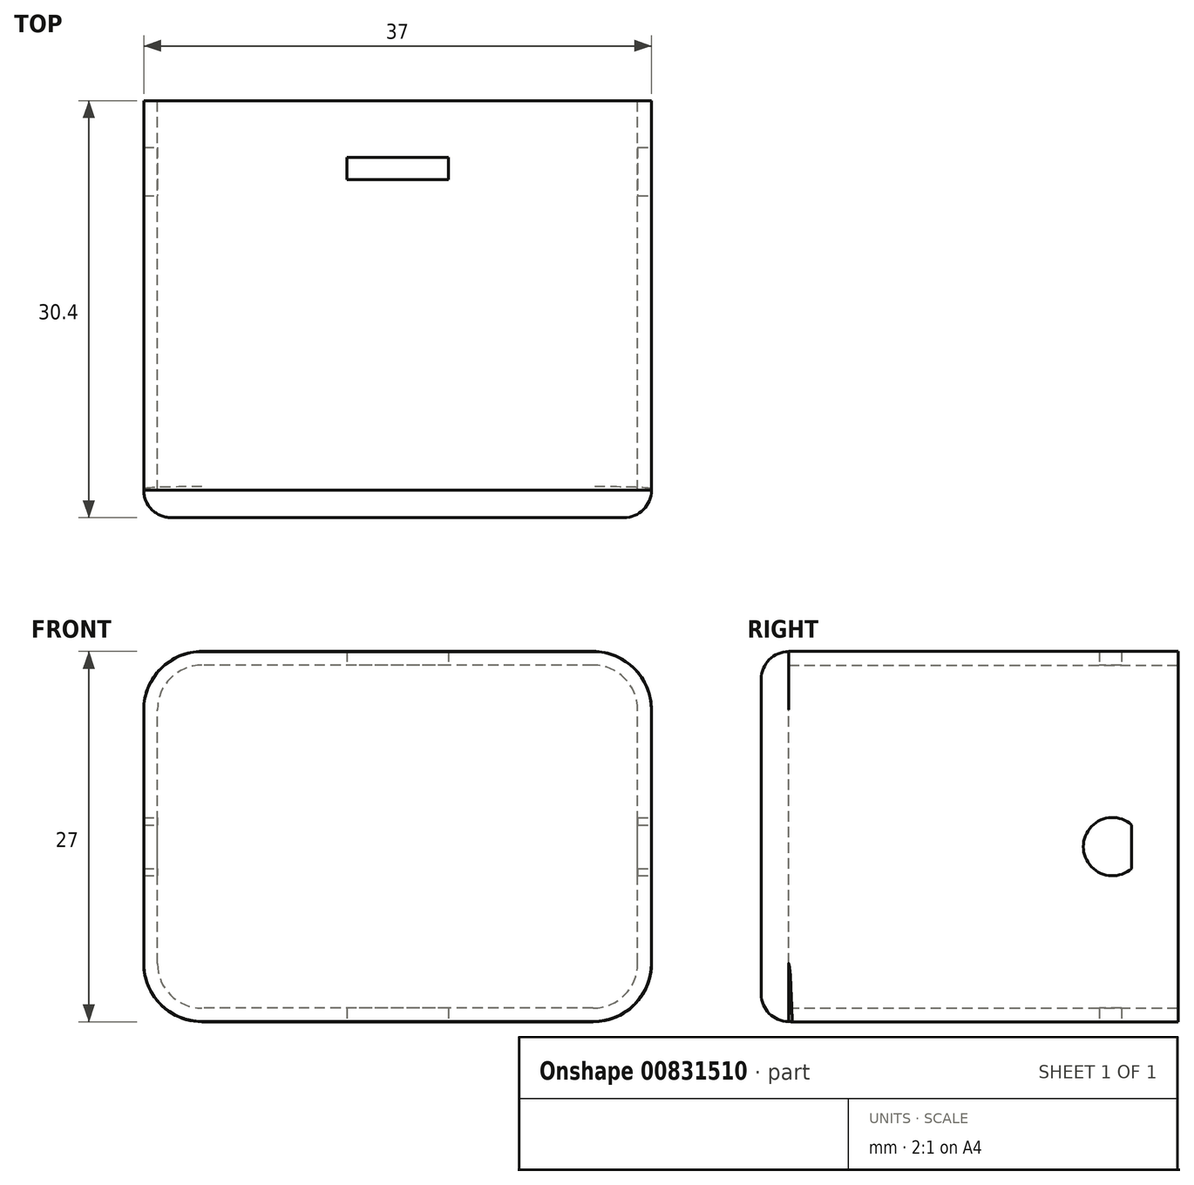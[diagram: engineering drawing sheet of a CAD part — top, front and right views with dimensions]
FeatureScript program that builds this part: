
annotation { "Feature Type Name" : "Feature", "Feature Type Description" : "" }
export const myFeature = defineFeature(function(context is Context, id is Id, definition is map)
    precondition{}
    {
        {
            var Q0;
            Q0=qCreatedBy(makeId("Front.planeOp"),FACE);
            var sketch = newSketch(context, id + "F0", { "sketchPlane" : qUnion([Q0])});
            skLineSegment(sketch, "E0.bottom", {"start": v(14.25, -12.5) * mm, "end": v(-14.25, -12.5) * mm});
            skLineSegment(sketch, "E0.top", {"start": v(14.25, 12.5) * mm, "end": v(-14.25, 12.5) * mm});
            skLineSegment(sketch, "E0.left", {"start": v(17.5, -9.25) * mm, "end": v(17.5, 9.25) * mm});
            skLineSegment(sketch, "E0.right", {"start": v(-17.5, -9.25) * mm, "end": v(-17.5, 9.25) * mm});
            skPoint(sketch, "E0.middle", {"position": v(0, 0) * mm});
            skPoint(sketch, "E1.visualSharp", {"position": v(-17.5, 12.5) * mm});
            skArc(sketch, "E1.filletArc", {"start": v(-14.25, 12.5) * mm, "mid": v(-16.55, 11.55) * mm, "end": v(-17.5, 9.25) * mm});
            skPoint(sketch, "E2.visualSharp", {"position": v(-17.5, -12.5) * mm});
            skArc(sketch, "E2.filletArc", {"start": v(-17.5, -9.25) * mm, "mid": v(-16.55, -11.55) * mm, "end": v(-14.25, -12.5) * mm});
            skPoint(sketch, "E3.visualSharp", {"position": v(17.5, -12.5) * mm});
            skArc(sketch, "E3.filletArc", {"start": v(14.25, -12.5) * mm, "mid": v(16.55, -11.55) * mm, "end": v(17.5, -9.25) * mm});
            skPoint(sketch, "E4.visualSharp", {"position": v(17.5, 12.5) * mm});
            skArc(sketch, "E4.filletArc", {"start": v(17.5, 9.25) * mm, "mid": v(16.55, 11.55) * mm, "end": v(14.25, 12.5) * mm});
            skLineSegment(sketch, "E5.0", {"start": v(14.25, -13.5) * mm, "end": v(-14.25, -13.5) * mm});
            skArc(sketch, "E5.1", {"start": v(-18.5, -9.25) * mm, "mid": v(-17.26, -12.26) * mm, "end": v(-14.25, -13.5) * mm});
            skArc(sketch, "E5.2", {"start": v(14.25, -13.5) * mm, "mid": v(17.26, -12.26) * mm, "end": v(18.5, -9.25) * mm});
            skLineSegment(sketch, "E5.3", {"start": v(-18.5, -9.25) * mm, "end": v(-18.5, 9.25) * mm});
            skLineSegment(sketch, "E5.4", {"start": v(18.5, -9.25) * mm, "end": v(18.5, 9.25) * mm});
            skArc(sketch, "E5.5", {"start": v(18.5, 9.25) * mm, "mid": v(17.26, 12.26) * mm, "end": v(14.25, 13.5) * mm});
            skLineSegment(sketch, "E5.6", {"start": v(14.25, 13.5) * mm, "end": v(-14.25, 13.5) * mm});
            skArc(sketch, "E5.7", {"start": v(-14.25, 13.5) * mm, "mid": v(-17.26, 12.26) * mm, "end": v(-18.5, 9.25) * mm});
            skSolve(sketch);
        }
        {
            var Q0;
            Q0 = qSketchRegion(id + "F0", true);
            extrude(context, id + "F1", {"entities" : qUnion([Q0]), "depth" : 25 * mm, "offsetDistance" : 25 * mm});
        }
        {
            var Q0;
            Q0=makeQuery(id+"F1.opExtrude","SWEPT_FACE",FACE,{"disambiguationData":[OSD([sQuery(id+"F0.wireOp",EDGE,"E5.0")])]});
            var sketch = newSketch(context, id + "F2", { "sketchPlane" : qUnion([Q0])});
            skLineSegment(sketch, "E6.bottom", {"start": v(3.7, 0.74) * mm, "end": v(-3.7, 0.74) * mm});
            skLineSegment(sketch, "E6.top", {"start": v(3.7, 2.34) * mm, "end": v(-3.7, 2.34) * mm});
            skLineSegment(sketch, "E6.left", {"start": v(3.7, 0.74) * mm, "end": v(3.7, 2.34) * mm});
            skLineSegment(sketch, "E6.right", {"start": v(-3.7, 0.74) * mm, "end": v(-3.7, 2.34) * mm});
            skPoint(sketch, "E6.middle", {"position": v(0, 1.54) * mm});
            skSolve(sketch);
        }
        {
            var Q0;
            Q0=makeQuery(id+"F2.imprint","IMPRINT",FACE,{"disambiguationData":[TD([[makeQuery(id+"F2.imprint","IMPRINT",EDGE,{"derivedFrom":sQuery(id+"F2.wireOp",EDGE,"E6.bottom")}),-1.0]])]});
            extrude(context, id + "F3", {"entities" : qUnion([Q0]), "operationType" : NewBodyOperationType.REMOVE, "endBound" : BoundingType.THROUGH_ALL, "oppositeDirection" : true, "depth" : 25 * mm, "offsetDistance" : 25 * mm});
        }
        {
            var Q0;
            Q0=qCreatedBy(makeId("Front.planeOp"),FACE);
            cPlane(context, id + "F4", {"entities" : qUnion([Q0]), "cplaneType" : CPlaneType.OFFSET, "offset" : 25 * mm, "width" : 150 * mm, "height" : 150 * mm});
        }
        {
            var Q0;
            Q0=qCreatedBy(id+"F4.planeOp",FACE);
            var sketch = newSketch(context, id + "F5", { "sketchPlane" : qUnion([Q0])});
            skLineSegment(sketch, "E7.bottom", {"start": v(14.25, -13.48) * mm, "end": v(-14.25, -13.48) * mm});
            skLineSegment(sketch, "E7.top", {"start": v(14.25, 13.48) * mm, "end": v(-14.25, 13.48) * mm});
            skLineSegment(sketch, "E7.left", {"start": v(18.5, -9.23) * mm, "end": v(18.5, 9.23) * mm});
            skLineSegment(sketch, "E7.right", {"start": v(-18.5, -9.23) * mm, "end": v(-18.5, 9.23) * mm});
            skPoint(sketch, "E7.middle", {"position": v(0, 0) * mm});
            skPoint(sketch, "E8.visualSharp", {"position": v(-18.5, 13.48) * mm});
            skArc(sketch, "E8.filletArc", {"start": v(-14.25, 13.48) * mm, "mid": v(-17.26, 12.24) * mm, "end": v(-18.5, 9.23) * mm});
            skPoint(sketch, "E9.visualSharp", {"position": v(18.5, 13.48) * mm});
            skArc(sketch, "E9.filletArc", {"start": v(18.5, 9.23) * mm, "mid": v(17.26, 12.24) * mm, "end": v(14.25, 13.48) * mm});
            skPoint(sketch, "E10.visualSharp", {"position": v(18.5, -13.48) * mm});
            skArc(sketch, "E10.filletArc", {"start": v(14.25, -13.48) * mm, "mid": v(17.26, -12.24) * mm, "end": v(18.5, -9.23) * mm});
            skPoint(sketch, "E11.visualSharp", {"position": v(-18.5, -13.48) * mm});
            skArc(sketch, "E11.filletArc", {"start": v(-18.5, -9.23) * mm, "mid": v(-17.26, -12.24) * mm, "end": v(-14.25, -13.48) * mm});
            skSolve(sketch);
        }
        {
            var Q0;
            Q0 = qSketchRegion(id + "F5", true);
            extrude(context, id + "F6", {"entities" : qUnion([Q0]), "operationType" : NewBodyOperationType.ADD, "depth" : 2 * mm, "offsetDistance" : 25 * mm});
        }
        {
            var Q0;
            Q0=makeQuery(id+"F6.opExtrude","CAP_EDGE",EDGE,{"disambiguationData":[OSD([sQuery(id+"F5.wireOp",EDGE,"E7.bottom")])],"isStart":false});
            var Q1;
            Q1=makeQuery(id+"F6.opExtrude","CAP_EDGE",EDGE,{"disambiguationData":[OSD([sQuery(id+"F5.wireOp",EDGE,"E10.filletArc")])],"isStart":false});
            var Q2;
            Q2=makeQuery(id+"F6.opExtrude","CAP_EDGE",EDGE,{"disambiguationData":[OSD([sQuery(id+"F5.wireOp",EDGE,"E7.left")])],"isStart":false});
            var Q3;
            Q3=makeQuery(id+"F6.opExtrude","CAP_EDGE",EDGE,{"disambiguationData":[OSD([sQuery(id+"F5.wireOp",EDGE,"E9.filletArc")])],"isStart":false});
            var Q4;
            Q4=makeQuery(id+"F6.opExtrude","CAP_EDGE",EDGE,{"disambiguationData":[OSD([sQuery(id+"F5.wireOp",EDGE,"E7.top")])],"isStart":false});
            var Q5;
            Q5=makeQuery(id+"F6.opExtrude","CAP_EDGE",EDGE,{"disambiguationData":[OSD([sQuery(id+"F5.wireOp",EDGE,"E8.filletArc")])],"isStart":false});
            var Q6;
            Q6=makeQuery(id+"F6.opExtrude","CAP_EDGE",EDGE,{"disambiguationData":[OSD([sQuery(id+"F5.wireOp",EDGE,"E7.right")])],"isStart":false});
            var Q7;
            Q7=makeQuery(id+"F1.opExtrude","CAP_EDGE",EDGE,{"disambiguationData":[OSD([sQuery(id+"F0.wireOp",EDGE,"E5.1")])],"isStart":false});
            fillet(context, id + "F7", {"entities" : qUnion([Q0, Q1, Q2, Q3, Q4, Q5, Q6, Q7]), "radius" : 2 * mm, "tangentPropagation" : true, "allowEdgeOverflow" : false});
        }
        {
            var Q0;
            Q0=makeQuery(id+"F0.imprint","IMPRINT",FACE,{"disambiguationData":[TD([[makeQuery(id+"F0.imprint","IMPRINT",EDGE,{"derivedFrom":sQuery(id+"F0.wireOp",EDGE,"E0.bottom")}),1.0]])]});
            extrude(context, id + "F8", {"entities" : qUnion([Q0]), "operationType" : NewBodyOperationType.ADD, "oppositeDirection" : true, "depth" : 3.4 * mm, "offsetDistance" : 25 * mm});
        }
        {
            var Q0;
            {var subQ0=sQuery(id+"F0.wireOp",EDGE,"E5.4");Q0=makeQuery(id+"F8.boolean.opBoolean","MERGE",FACE,{"derivedFrom":[makeQuery(id+"F6.boolean.opBoolean","MERGE",FACE,{"derivedFrom":[makeQuery(id+"F1.opExtrude","SWEPT_FACE",FACE,{"disambiguationData":[OSD([subQ0])]}),makeQuery(id+"F6.opExtrude","SWEPT_FACE",FACE,{"disambiguationData":[OSD([sQuery(id+"F5.wireOp",EDGE,"E7.left")])]})]}),makeQuery(id+"F8.opExtrude","SWEPT_FACE",FACE,{"disambiguationData":[OSD([subQ0])]})]});}
            var sketch = newSketch(context, id + "F9", { "sketchPlane" : qUnion([Q0])});
            skArc(sketch, "E12", {"start": v(0, 0.85) * mm, "mid": v(-3.53, -0.74) * mm, "end": v(0, -2.32) * mm});
            skLineSegment(sketch, "E13", {"start": v(0, 0.85) * mm, "end": v(0, -2.32) * mm});
            skArc(sketch, "E14.0", {"start": v(0.66, 1.6) * mm, "mid": v(-4.53, -0.74) * mm, "end": v(0.66, -3.07) * mm});
            skSolve(sketch);
        }
        {
            var Q0;
            Q0=makeQuery(id+"F9.imprint","IMPRINT",FACE,{"disambiguationData":[TD([[makeQuery(id+"F9.imprint","IMPRINT",EDGE,{"derivedFrom":sQuery(id+"F9.wireOp",EDGE,"E12")}),1.0]])]});
            extrude(context, id + "F10", {"entities" : qUnion([Q0]), "operationType" : NewBodyOperationType.REMOVE, "oppositeDirection" : true, "depth" : 46.3 * mm, "offsetDistance" : 25 * mm});
        }
    });
